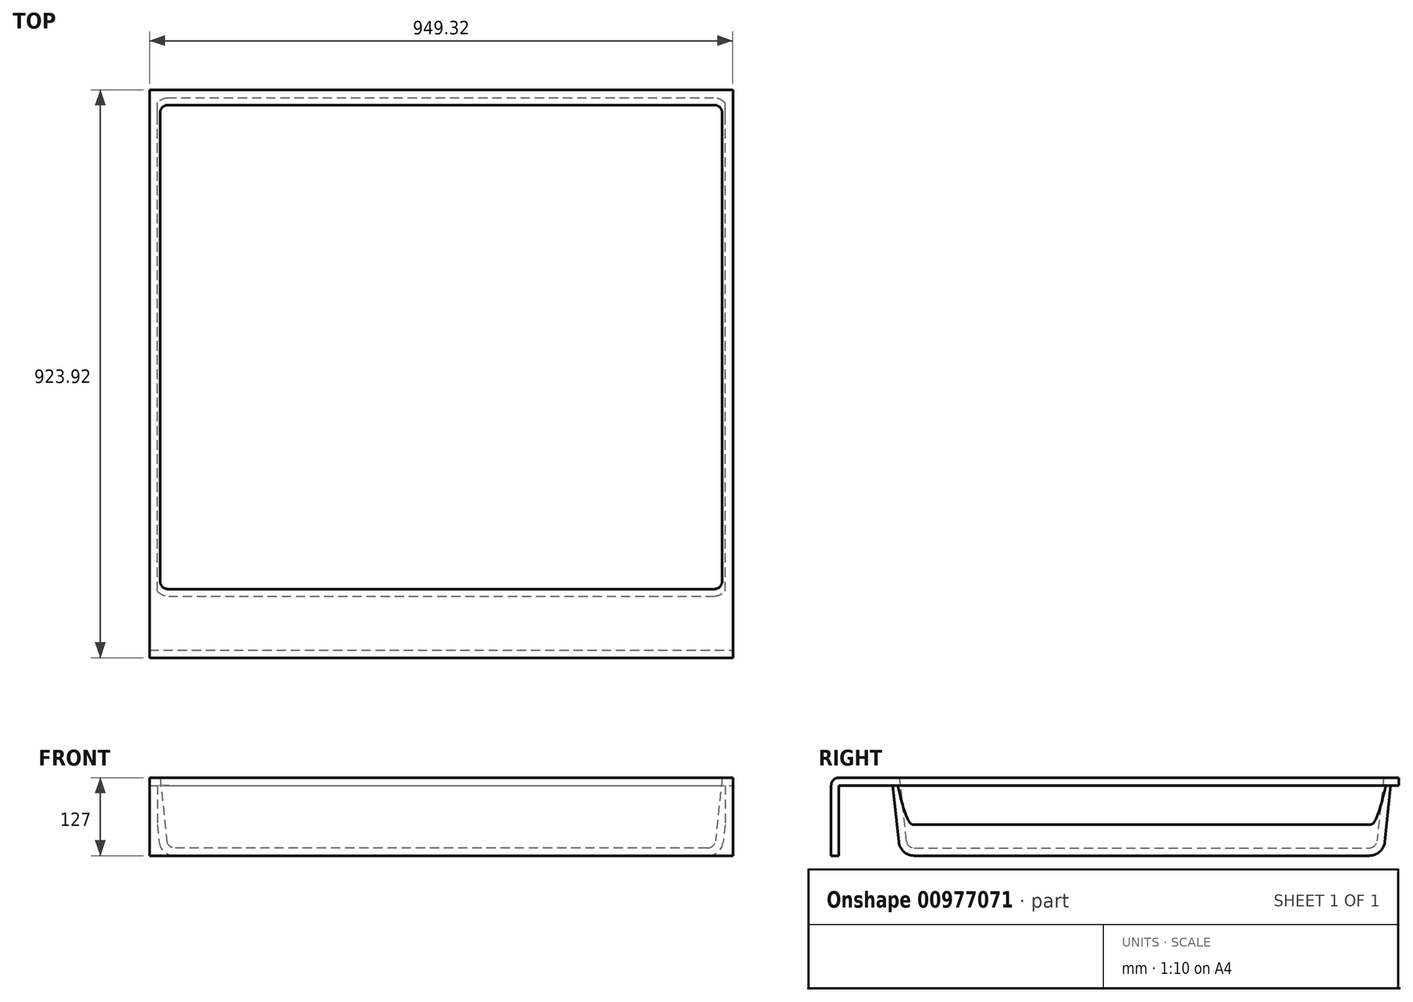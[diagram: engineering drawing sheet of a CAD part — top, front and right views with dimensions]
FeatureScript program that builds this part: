
annotation { "Feature Type Name" : "Feature", "Feature Type Description" : "" }
export const myFeature = defineFeature(function(context is Context, id is Id, definition is map)
    precondition{}
    {
        {
            var Q0;
            Q0=qCreatedBy(makeId("Top.planeOp"),FACE);
            var sketch = newSketch(context, id + "F0", { "sketchPlane" : qUnion([Q0])});
            skLineSegment(sketch, "E0.bottom", {"start": v(0, 0) * mm, "end": v(949.33, 0) * mm});
            skLineSegment(sketch, "E0.top", {"start": v(0, -923.93) * mm, "end": v(949.33, -923.93) * mm});
            skLineSegment(sketch, "E0.left", {"start": v(0, 0) * mm, "end": v(0, -923.93) * mm});
            skLineSegment(sketch, "E0.right", {"start": v(949.33, 0) * mm, "end": v(949.33, -923.93) * mm});
            skSolve(sketch);
        }
        {
            var Q0;
            Q0=makeQuery(id+"F0.imprint","IMPRINT",FACE,{"disambiguationData":[TD([[makeQuery(id+"F0.imprint","IMPRINT",EDGE,{"derivedFrom":sQuery(id+"F0.wireOp",EDGE,"E0.bottom")}),-1.0]])]});
            extrude(context, id + "F1", {"entities" : qUnion([Q0]), "depth" : 127 * mm, "offsetDistance" : 25.4 * mm});
        }
        {
            var Q0;
            Q0=makeQuery(id+"F1.opExtrude","CAP_FACE",FACE,{"disambiguationData":[OSD([sQuery(id+"F0.wireOp",EDGE,"E0.bottom"),sQuery(id+"F0.wireOp",EDGE,"E0.top"),sQuery(id+"F0.wireOp",EDGE,"E0.left"),sQuery(id+"F0.wireOp",EDGE,"E0.right")])],"isStart":false});
            var sketch = newSketch(context, id + "F2", { "sketchPlane" : qUnion([Q0])});
            skLineSegment(sketch, "E1.bottom", {"start": v(17.46, -812.22) * mm, "end": v(931.86, -812.22) * mm});
            skLineSegment(sketch, "E1.top", {"start": v(17.46, -24.82) * mm, "end": v(931.86, -24.82) * mm});
            skLineSegment(sketch, "E1.left", {"start": v(17.46, -812.22) * mm, "end": v(17.46, -24.82) * mm});
            skLineSegment(sketch, "E1.right", {"start": v(931.86, -812.22) * mm, "end": v(931.86, -24.82) * mm});
            skSolve(sketch);
        }
        {
            var Q0;
            Q0=makeQuery(id+"F2.imprint","IMPRINT",FACE,{"disambiguationData":[TD([[makeQuery(id+"F2.imprint","IMPRINT",EDGE,{"derivedFrom":sQuery(id+"F2.wireOp",EDGE,"E1.bottom")}),1.0]])]});
            extrude(context, id + "F3", {"entities" : qUnion([Q0]), "operationType" : NewBodyOperationType.REMOVE, "oppositeDirection" : true, "depth" : 114.3 * mm, "offsetDistance" : 25.4 * mm, "hasDraft" : true, "draftAngle" : 6 * degree, "draftPullDirection" : true});
        }
        {
            var Q0;
            Q0=makeQuery(id+"F3.boolean.opBoolean","COPY",EDGE,{"derivedFrom":makeQuery(id+"F3.opExtrude","CAP_EDGE",EDGE,{"disambiguationData":[OSD([sQuery(id+"F2.wireOp",EDGE,"E1.left")])],"isStart":false})});
            var Q1;
            Q1=makeQuery(id+"F3.boolean.opBoolean","COPY",EDGE,{"derivedFrom":makeQuery(id+"F3.opExtrude","SWEPT_EDGE",EDGE,{"disambiguationData":[OSD([sQuery(id+"F2.wireOp",EDGE,"E1.bottom"),sQuery(id+"F2.wireOp",EDGE,"E1.left")])]})});
            var Q2;
            Q2=makeQuery(id+"F3.boolean.opBoolean","COPY",EDGE,{"derivedFrom":makeQuery(id+"F3.opExtrude","CAP_EDGE",EDGE,{"disambiguationData":[OSD([sQuery(id+"F2.wireOp",EDGE,"E1.left")])],"isStart":true})});
            var Q3;
            Q3=makeQuery(id+"F3.boolean.opBoolean","COPY",EDGE,{"derivedFrom":makeQuery(id+"F3.opExtrude","CAP_EDGE",EDGE,{"disambiguationData":[OSD([sQuery(id+"F2.wireOp",EDGE,"E1.bottom")])],"isStart":true})});
            var Q4;
            Q4=makeQuery(id+"F3.boolean.opBoolean","COPY",EDGE,{"derivedFrom":makeQuery(id+"F3.opExtrude","CAP_EDGE",EDGE,{"disambiguationData":[OSD([sQuery(id+"F2.wireOp",EDGE,"E1.bottom")])],"isStart":false})});
            var Q5;
            Q5=makeQuery(id+"F3.boolean.opBoolean","COPY",EDGE,{"derivedFrom":makeQuery(id+"F3.opExtrude","CAP_EDGE",EDGE,{"disambiguationData":[OSD([sQuery(id+"F2.wireOp",EDGE,"E1.right")])],"isStart":false})});
            var Q6;
            Q6=makeQuery(id+"F3.boolean.opBoolean","COPY",EDGE,{"derivedFrom":makeQuery(id+"F3.opExtrude","SWEPT_EDGE",EDGE,{"disambiguationData":[OSD([sQuery(id+"F2.wireOp",EDGE,"E1.bottom"),sQuery(id+"F2.wireOp",EDGE,"E1.right")])]})});
            var Q7;
            Q7=makeQuery(id+"F3.boolean.opBoolean","COPY",EDGE,{"derivedFrom":makeQuery(id+"F3.opExtrude","SWEPT_EDGE",EDGE,{"disambiguationData":[OSD([sQuery(id+"F2.wireOp",EDGE,"E1.top"),sQuery(id+"F2.wireOp",EDGE,"E1.right")])]})});
            var Q8;
            Q8=makeQuery(id+"F3.boolean.opBoolean","COPY",EDGE,{"derivedFrom":makeQuery(id+"F3.opExtrude","CAP_EDGE",EDGE,{"disambiguationData":[OSD([sQuery(id+"F2.wireOp",EDGE,"E1.top")])],"isStart":false})});
            var Q9;
            Q9=makeQuery(id+"F3.boolean.opBoolean","COPY",EDGE,{"derivedFrom":makeQuery(id+"F3.opExtrude","CAP_EDGE",EDGE,{"disambiguationData":[OSD([sQuery(id+"F2.wireOp",EDGE,"E1.top")])],"isStart":true})});
            var Q10;
            Q10=makeQuery(id+"F3.boolean.opBoolean","COPY",EDGE,{"derivedFrom":makeQuery(id+"F3.opExtrude","SWEPT_EDGE",EDGE,{"disambiguationData":[OSD([sQuery(id+"F2.wireOp",EDGE,"E1.top"),sQuery(id+"F2.wireOp",EDGE,"E1.left")])]})});
            fillet(context, id + "F4", {"entities" : qUnion([Q0, Q1, Q2, Q3, Q4, Q5, Q6, Q7, Q8, Q9, Q10]), "radius" : 12.7 * mm, "tangentPropagation" : true, "allowEdgeOverflow" : false});
        }
        {
            var Q0;
            Q0=makeQuery(id+"F1.opExtrude","CAP_EDGE",EDGE,{"disambiguationData":[OSD([sQuery(id+"F0.wireOp",EDGE,"E0.top")])],"isStart":false});
            fillet(context, id + "F5", {"entities" : qUnion([Q0]), "radius" : 12.7 * mm, "tangentPropagation" : true, "allowEdgeOverflow" : false});
        }
        {
            var Q0;
            Q0=makeQuery(id+"F1.opExtrude","CAP_FACE",FACE,{"disambiguationData":[OSD([sQuery(id+"F0.wireOp",EDGE,"E0.bottom"),sQuery(id+"F0.wireOp",EDGE,"E0.top"),sQuery(id+"F0.wireOp",EDGE,"E0.left"),sQuery(id+"F0.wireOp",EDGE,"E0.right")])],"isStart":true});
            shell(context, id + "F6", {"entities" : qUnion([Q0]), "thickness" : 12.7 * mm});
        }
        {
            var Q0;
            Q0=makeQuery(id+"F1.opExtrude","SWEPT_FACE",FACE,{"disambiguationData":[OSD([sQuery(id+"F0.wireOp",EDGE,"E0.right")])]});
            var sketch = newSketch(context, id + "F7", { "sketchPlane" : qUnion([Q0])});
            skLineSegment(sketch, "E2.bottom", {"start": v(-911.23, 114.3) * mm, "end": v(0, 114.3) * mm});
            skLineSegment(sketch, "E2.top", {"start": v(-911.23, 0) * mm, "end": v(0, 0) * mm});
            skLineSegment(sketch, "E2.left", {"start": v(-911.23, 114.3) * mm, "end": v(-911.23, 0) * mm});
            skLineSegment(sketch, "E2.right", {"start": v(0, 114.3) * mm, "end": v(0, 0) * mm});
            skSolve(sketch);
        }
        {
            var Q0;
            Q0=makeQuery(id+"F7.imprint","IMPRINT",FACE,{"disambiguationData":[TD([[makeQuery(id+"F7.imprint","IMPRINT",EDGE,{"derivedFrom":sQuery(id+"F7.wireOp",EDGE,"E2.bottom")}),-1.0]])]});
            extrude(context, id + "F8", {"entities" : qUnion([Q0]), "operationType" : NewBodyOperationType.REMOVE, "oppositeDirection" : true, "depth" : 12.7 * mm, "offsetDistance" : 25.4 * mm});
        }
        {
            var Q0;
            Q0=makeQuery(id+"F1.opExtrude","SWEPT_FACE",FACE,{"disambiguationData":[OSD([sQuery(id+"F0.wireOp",EDGE,"E0.bottom")])]});
            var sketch = newSketch(context, id + "F9", { "sketchPlane" : qUnion([Q0])});
            skLineSegment(sketch, "E3", {"start": v(-936.63, 114.3) * mm, "end": v(0, 114.3) * mm});
            skSolve(sketch);
        }
        {
            var Q0;
            {var subQ0=sQuery(id+"F9.wireOp",EDGE,"E3");Q0=makeQuery(id+"F9.imprint","IMPRINT",FACE,{"disambiguationData":[TD([[makeQuery(id+"F9.imprint","IMPRINT",EDGE,{"derivedFrom":subQ0}),-1.0]])]});}
            extrude(context, id + "F10", {"entities" : qUnion([Q0]), "operationType" : NewBodyOperationType.REMOVE, "oppositeDirection" : true, "depth" : 12.7 * mm, "offsetDistance" : 25.4 * mm});
        }
        {
            var Q0;
            Q0=makeQuery(id+"F1.opExtrude","SWEPT_FACE",FACE,{"disambiguationData":[OSD([sQuery(id+"F0.wireOp",EDGE,"E0.left")])]});
            var sketch = newSketch(context, id + "F11", { "sketchPlane" : qUnion([Q0])});
            skLineSegment(sketch, "E4.bottom", {"start": v(911.23, 114.3) * mm, "end": v(12.7, 114.3) * mm});
            skLineSegment(sketch, "E4.top", {"start": v(911.23, 0) * mm, "end": v(12.7, 0) * mm});
            skLineSegment(sketch, "E4.left", {"start": v(911.23, 114.3) * mm, "end": v(911.23, 0) * mm});
            skLineSegment(sketch, "E4.right", {"start": v(12.7, 114.3) * mm, "end": v(12.7, 0) * mm});
            skSolve(sketch);
        }
        {
            var Q0;
            Q0=makeQuery(id+"F11.imprint","IMPRINT",FACE,{"disambiguationData":[TD([[makeQuery(id+"F11.imprint","IMPRINT",EDGE,{"derivedFrom":sQuery(id+"F11.wireOp",EDGE,"E4.bottom")}),1.0]])]});
            extrude(context, id + "F12", {"entities" : qUnion([Q0]), "operationType" : NewBodyOperationType.REMOVE, "oppositeDirection" : true, "depth" : 12.7 * mm, "offsetDistance" : 25.4 * mm});
        }
    });
